# Revit family: FP_Revit_18_RB2470BLV1_Fridge_90001121A
name_source: partatom
category: Specialty Equipment
revit_build: Autodesk Revit 2018 (Build: 20170223_1515(x64)
units: mm (PartAtom-declared; Revit-internal decimal feet)

## family parameters
Always vertical = Yes
Cut with Voids When Loaded = Yes
OmniClass Number = 23.40.40.11.11.17
OmniClass Title = Refrigerator-Freezer
Part Type = Normal
Room Calculation Point = No
Round Connector Dimension = Use Diameter
Shared = No
Work Plane-Based = No

## types (1)
- FP_Revit_18_RB2470BLV1_Fridge_90001121A
    Cavity - Depth = 550 mm
    Cavity - Height (1782mm to 1786mm) = 1786 mm  [stored 5.85958 ft]
    Cavity - Width (564mm - 570mm) = 570 mm  [stored 1.87008 ft]
    Chassis - Depth = 560 mm  [stored 1.83727 ft]
    Chassis - Height = 1662 mm  [stored 5.45276 ft]
    Chassis - Width = 790 mm  [stored 2.59186 ft]
    Connector Description - Electrical = 120 V, 60Hz, 10 A, fused electrical supply
    Description = 24" Integrated Refrigerator Freezer
    Floor Offset 18mm = 18 mm  [stored 0.0590551 ft]
    Handle Offset (R=39mm - L=516mm) = 516 mm  [stored 1.69291 ft]
    Handle Style - Contemporary Round (AHSRD70B) = No
    Handle Style - Contemporary Square (AHD3RD70B) = No
    Manufacturer = Fisher & Paykel Appliances
    Material - Body = Fisher & Paykel - Grey
    Material - Door Front = Fisher & Paykel - Stainless Steel
    Material - Door Structure = Fisher & Paykel - White
    Model = RB2470BLV1
    Product - Depth = 540 mm  [stored 1.77165 ft]
    Product - Height = 1773 mm  [stored 5.81693 ft]
    Product - Width = 555 mm  [stored 1.82087 ft]
    Stainless Steel Door Panels (RD2470BL) = No
    URL = www.fisherpaykel.com
    Visibility - Clearance Required = Yes

note: [stored X ft] marks values corroborated as IEEE doubles in the binary element streams (Revit-internal decimal feet)

## geometry (parser evidence)
native form markers: Sweep x8
no freeform markers — native parametric forms only
